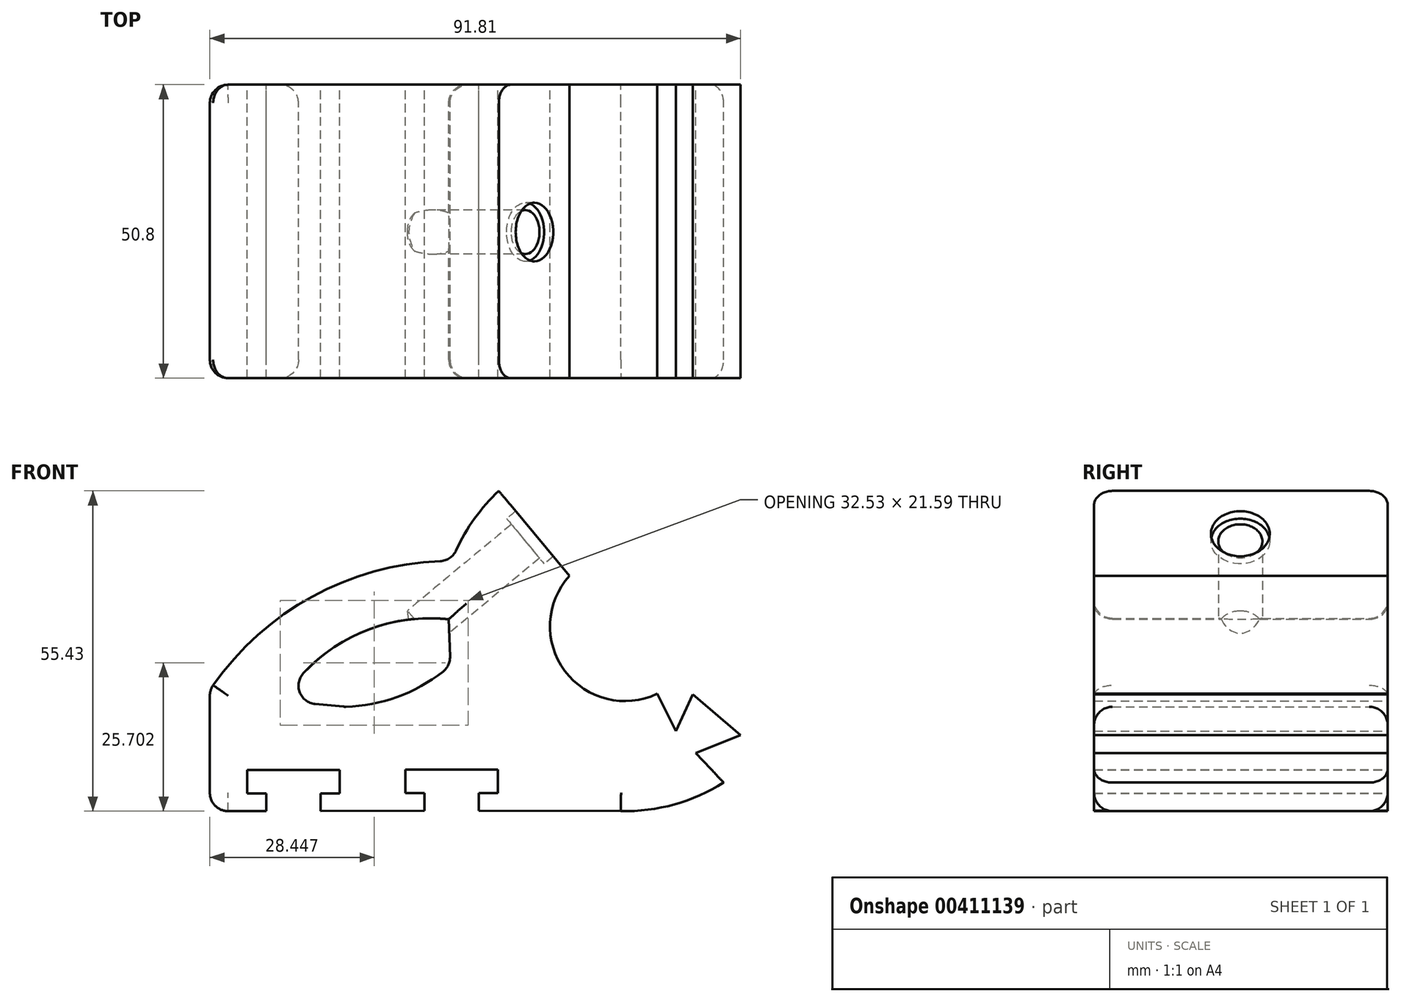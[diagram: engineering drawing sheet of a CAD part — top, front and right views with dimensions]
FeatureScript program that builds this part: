
annotation { "Feature Type Name" : "Feature", "Feature Type Description" : "" }
export const myFeature = defineFeature(function(context is Context, id is Id, definition is map)
    precondition{}
    {
        {
            var Q0;
            Q0=qCreatedBy(makeId("Front.planeOp"),FACE);
            var sketch = newSketch(context, id + "F0", { "sketchPlane" : qUnion([Q0])});
            skArc(sketch, "E0", {"start": v(-9.59, 8.71) * mm, "mid": v(8.71, -9.59) * mm, "end": v(-7.76, 10.37) * mm});
            skArc(sketch, "E1", {"start": v(-0.7, -32) * mm, "mid": v(30.35, 10.16) * mm, "end": v(-19.84, 25.12) * mm});
            skLineSegment(sketch, "E2", {"start": v(17.09, -27.06) * mm, "end": v(12.28, -21.97) * mm});
            skLineSegment(sketch, "E3", {"start": v(12.28, -21.97) * mm, "end": v(20, -18.82) * mm});
            skLineSegment(sketch, "E4", {"start": v(20, -18.82) * mm, "end": v(11.77, -11.8) * mm});
            skLineSegment(sketch, "E5", {"start": v(11.77, -11.8) * mm, "end": v(8.83, -18.14) * mm});
            skLineSegment(sketch, "E6", {"start": v(8.83, -18.14) * mm, "end": v(5.57, -11.7) * mm});
            skLineSegment(sketch, "E7", {"start": v(-21.81, 23.42) * mm, "end": v(-9.59, 8.71) * mm});
            skLineSegment(sketch, "E8", {"start": v(-19.84, 25.12) * mm, "end": v(-7.76, 10.37) * mm});
            skArc(sketch, "E9.trimOffspring", {"start": v(-21.81, 23.42) * mm, "mid": v(-26.58, 17.83) * mm, "end": v(-29.94, 11.3) * mm});
            skLineSegment(sketch, "E10.left", {"start": v(-71.8, -11.06) * mm, "end": v(-71.8, -32.02) * mm});
            skLineSegment(sketch, "E11.left", {"start": v(-34.66, -28.86) * mm, "end": v(-34.66, -31.9) * mm});
            skLineSegment(sketch, "E11.right", {"start": v(-25.26, -28.87) * mm, "end": v(-25.26, -31.91) * mm});
            skLineSegment(sketch, "E12.bottom", {"start": v(-37.96, -24.8) * mm, "end": v(-21.96, -24.8) * mm});
            skLineSegment(sketch, "E12.left", {"start": v(-37.96, -24.8) * mm, "end": v(-37.96, -28.86) * mm});
            skLineSegment(sketch, "E12.right", {"start": v(-21.96, -24.8) * mm, "end": v(-21.96, -28.86) * mm});
            skLineSegment(sketch, "E13", {"start": v(-34.66, -28.86) * mm, "end": v(-37.96, -28.86) * mm});
            skLineSegment(sketch, "E14", {"start": v(-25.26, -28.87) * mm, "end": v(-21.96, -28.86) * mm});
            skLineSegment(sketch, "E15", {"start": v(-34.66, -31.9) * mm, "end": v(-52.67, -31.96) * mm});
            skLineSegment(sketch, "E16", {"start": v(-25.26, -31.91) * mm, "end": v(-0.7, -32) * mm});
            skLineSegment(sketch, "E17.left", {"start": v(-62.07, -28.94) * mm, "end": v(-62.07, -31.99) * mm});
            skLineSegment(sketch, "E17.right", {"start": v(-52.67, -28.91) * mm, "end": v(-52.67, -31.96) * mm});
            skLineSegment(sketch, "E18.bottom", {"start": v(-65.37, -24.88) * mm, "end": v(-49.37, -24.85) * mm});
            skLineSegment(sketch, "E18.left", {"start": v(-65.37, -24.88) * mm, "end": v(-65.37, -28.94) * mm});
            skLineSegment(sketch, "E18.right", {"start": v(-49.37, -24.85) * mm, "end": v(-49.37, -28.91) * mm});
            skLineSegment(sketch, "E19", {"start": v(-62.07, -28.94) * mm, "end": v(-65.37, -28.94) * mm});
            skLineSegment(sketch, "E20", {"start": v(-52.67, -28.91) * mm, "end": v(-49.37, -28.91) * mm});
            skLineSegment(sketch, "E21.trimOffspring", {"start": v(-62.07, -31.99) * mm, "end": v(-71.8, -32.02) * mm});
            skArc(sketch, "E22", {"start": v(-29.94, 11.3) * mm, "mid": v(-53.67, 5.37) * mm, "end": v(-71.8, -11.06) * mm});
            skArc(sketch, "E23", {"start": v(-30.48, 1.2) * mm, "mid": v(-46.92, -1.69) * mm, "end": v(-59.26, -12.91) * mm});
            skArc(sketch, "E24", {"start": v(-48.5, -13.93) * mm, "mid": v(-38.71, -11.99) * mm, "end": v(-30.2, -6.79) * mm});
            skLineSegment(sketch, "E25", {"start": v(-30.48, 1.2) * mm, "end": v(-30.2, -6.79) * mm});
            skLineSegment(sketch, "E26", {"start": v(-59.26, -12.91) * mm, "end": v(-48.5, -13.93) * mm});
            skSolve(sketch);
        }
        {
            var Q0;
            {var subQ1=sQuery(id+"F0.wireOp",EDGE,"E2");Q0=makeQuery(id+"F0.imprint","IMPRINT",FACE,{"disambiguationData":[TD([[makeQuery(id+"F0.imprint","IMPRINT",EDGE,{"derivedFrom":subQ1}),1.0]])]});}
            extrude(context, id + "F1", {"entities" : qUnion([Q0]), "depth" : 50.8 * mm});
        }
        {
            var Q0;
            Q0=makeQuery(id+"F1.opExtrude","SWEPT_FACE",FACE,{"disambiguationData":[OSD([sQuery(id+"F0.wireOp",EDGE,"E7")])]});
            var sketch = newSketch(context, id + "F2", { "sketchPlane" : qUnion([Q0])});
            skPoint(sketch, "E27", {"position": v(-25.5, 22.32) * mm});
            skSolve(sketch);
        }
        {
            var Q0;
            Q0=sQuery(id+"F2.wireOp",VERTEX,"E27");
            var Q1;
            Q1=makeQuery(id+"F1.opExtrude","SWEPT_BODY",BODY,{"disambiguationData":[OSD([sQuery(id+"F0.wireOp",EDGE,"E0"),sQuery(id+"F0.wireOp",EDGE,"E1"),sQuery(id+"F0.wireOp",EDGE,"B8RJHwGn-14ZO-HIs1-wqbf-50VYlL9qGnVK.bottom"),sQuery(id+"F0.wireOp",EDGE,"E2"),sQuery(id+"F0.wireOp",EDGE,"E3"),sQuery(id+"F0.wireOp",EDGE,"E4"),sQuery(id+"F0.wireOp",EDGE,"E5"),sQuery(id+"F0.wireOp",EDGE,"E6"),sQuery(id+"F0.wireOp",EDGE,"E7"),sQuery(id+"F0.wireOp",EDGE,"E9.trimOffspring"),sQuery(id+"F0.wireOp",EDGE,"E10.left"),sQuery(id+"F0.wireOp",EDGE,"E11.left"),sQuery(id+"F0.wireOp",EDGE,"E11.right"),sQuery(id+"F0.wireOp",EDGE,"E12.bottom"),sQuery(id+"F0.wireOp",EDGE,"E12.left"),sQuery(id+"F0.wireOp",EDGE,"E12.right"),sQuery(id+"F0.wireOp",EDGE,"E13"),sQuery(id+"F0.wireOp",EDGE,"E14"),sQuery(id+"F0.wireOp",EDGE,"E15"),sQuery(id+"F0.wireOp",EDGE,"E16"),sQuery(id+"F0.wireOp",EDGE,"E17.left"),sQuery(id+"F0.wireOp",EDGE,"E17.right"),sQuery(id+"F0.wireOp",EDGE,"E18.bottom"),sQuery(id+"F0.wireOp",EDGE,"E18.left"),sQuery(id+"F0.wireOp",EDGE,"E18.right"),sQuery(id+"F0.wireOp",EDGE,"E19"),sQuery(id+"F0.wireOp",EDGE,"E20"),sQuery(id+"F0.wireOp",EDGE,"E21.trimOffspring")])]});
            hole(context, id + "F3", {"style" : HoleStyle.C_BORE, "endStyle" : HoleEndStyle.BLIND, "holeDiameter" : 7.62 * mm, "cBoreDiameter" : 10.16 * mm, "cBoreDepth" : 2.03 * mm, "holeDepth" : 25.4 * mm, "isTappedThrough" : true, "tappedDepth" : 12.7 * mm, "tapClearance" : 3, "locations" : qUnion([Q0]), "scope" : qUnion([Q1]), "startStyle" : HoleStartStyle.PART});
        }
        {
            var Q0;
            Q0=makeQuery(id+"F1.opExtrude","SWEPT_EDGE",EDGE,{"disambiguationData":[OSD([sQuery(id+"F0.wireOp",EDGE,"E9.trimOffspring"),sQuery(id+"F0.wireOp",EDGE,"E22")])]});
            var Q1;
            Q1=makeQuery(id+"F1.opExtrude","SWEPT_EDGE",EDGE,{"disambiguationData":[OSD([sQuery(id+"F0.wireOp",EDGE,"E23"),sQuery(id+"F0.wireOp",EDGE,"E26")])]});
            var Q2;
            Q2=makeQuery(id+"F1.opExtrude","SWEPT_EDGE",EDGE,{"disambiguationData":[OSD([sQuery(id+"F0.wireOp",EDGE,"E24"),sQuery(id+"F0.wireOp",EDGE,"E25")])]});
            var Q3;
            Q3=makeQuery(id+"F1.opExtrude","SWEPT_EDGE",EDGE,{"disambiguationData":[OSD([sQuery(id+"F0.wireOp",EDGE,"E24"),sQuery(id+"F0.wireOp",EDGE,"E26")])]});
            fillet(context, id + "F4", {"entities" : qUnion([Q0, Q1, Q2, Q3]), "radius" : 3.17 * mm, "tangentPropagation" : true, "allowEdgeOverflow" : false});
        }
        {
            var Q0;
            Q0=makeQuery(id+"F1.opExtrude","CAP_EDGE",EDGE,{"disambiguationData":[OSD([sQuery(id+"F0.wireOp",EDGE,"E9.trimOffspring")])],"isStart":false});
            var Q1;
            Q1=makeQuery(id+"F1.opExtrude","CAP_EDGE",EDGE,{"disambiguationData":[OSD([sQuery(id+"F0.wireOp",EDGE,"E9.trimOffspring")])],"isStart":true});
            var Q2;
            Q2=makeQuery(id+"F1.opExtrude","CAP_EDGE",EDGE,{"disambiguationData":[OSD([sQuery(id+"F0.wireOp",EDGE,"E1")])],"isStart":false});
            var Q3;
            Q3=makeQuery(id+"F1.opExtrude","CAP_EDGE",EDGE,{"disambiguationData":[OSD([sQuery(id+"F0.wireOp",EDGE,"E1")])],"isStart":true});
            var Q4;
            Q4=makeQuery(id+"F1.opExtrude","SWEPT_EDGE",EDGE,{"disambiguationData":[OSD([sQuery(id+"F0.wireOp",EDGE,"E10.left"),sQuery(id+"F0.wireOp",EDGE,"E21.trimOffspring")])]});
            fillet(context, id + "F5", {"entities" : qUnion([Q0, Q1, Q2, Q3, Q4]), "radius" : 3.17 * mm, "tangentPropagation" : true, "allowEdgeOverflow" : false});
        }
        {
            var Q0;
            Q0=makeQuery(id+"F1.opExtrude","CAP_EDGE",EDGE,{"disambiguationData":[OSD([sQuery(id+"F0.wireOp",EDGE,"E23")])],"isStart":false});
            var Q1;
            Q1=makeQuery(id+"F1.opExtrude","CAP_EDGE",EDGE,{"disambiguationData":[OSD([sQuery(id+"F0.wireOp",EDGE,"E23")])],"isStart":true});
            var Q2;
            Q2=makeQuery(id+"F1.opExtrude","CAP_EDGE",EDGE,{"disambiguationData":[OSD([sQuery(id+"F0.wireOp",EDGE,"E10.left")])],"isStart":false});
            fillet(context, id + "F6", {"entities" : qUnion([Q0, Q1, Q2]), "radius" : 3.17 * mm, "tangentPropagation" : true, "allowEdgeOverflow" : false});
        }
    });
